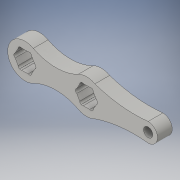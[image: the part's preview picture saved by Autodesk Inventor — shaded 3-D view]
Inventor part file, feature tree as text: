
AUTODESK INVENTOR PART (.ipt)
format: ipt  version: 2016 (Build 200138000, 138)  size: 176,640 bytes
history: native  units: in
note: dims shown in document units (in); Inventor stores cm internally (conversion verified against a paired STEP export)
features: extrude x1, sketch x1
ambient origin geometry x8: Origin, YZ Plane, XZ Plane, XY Plane, X Axis, Y Axis, Z Axis, Center Point
bodies: Solid1 (feature_tree)
feature tree (2):
  extrude  "Extrusion1"  Depth=0.6in
  sketch  "Sketch1"  dims[d6=0.78in d19=0.375in d20=1.4in d21=0.76in d22=5.0in d23=5.0in d24=2.0in d25=2.0in d26=0.6in d27=0.0in]
